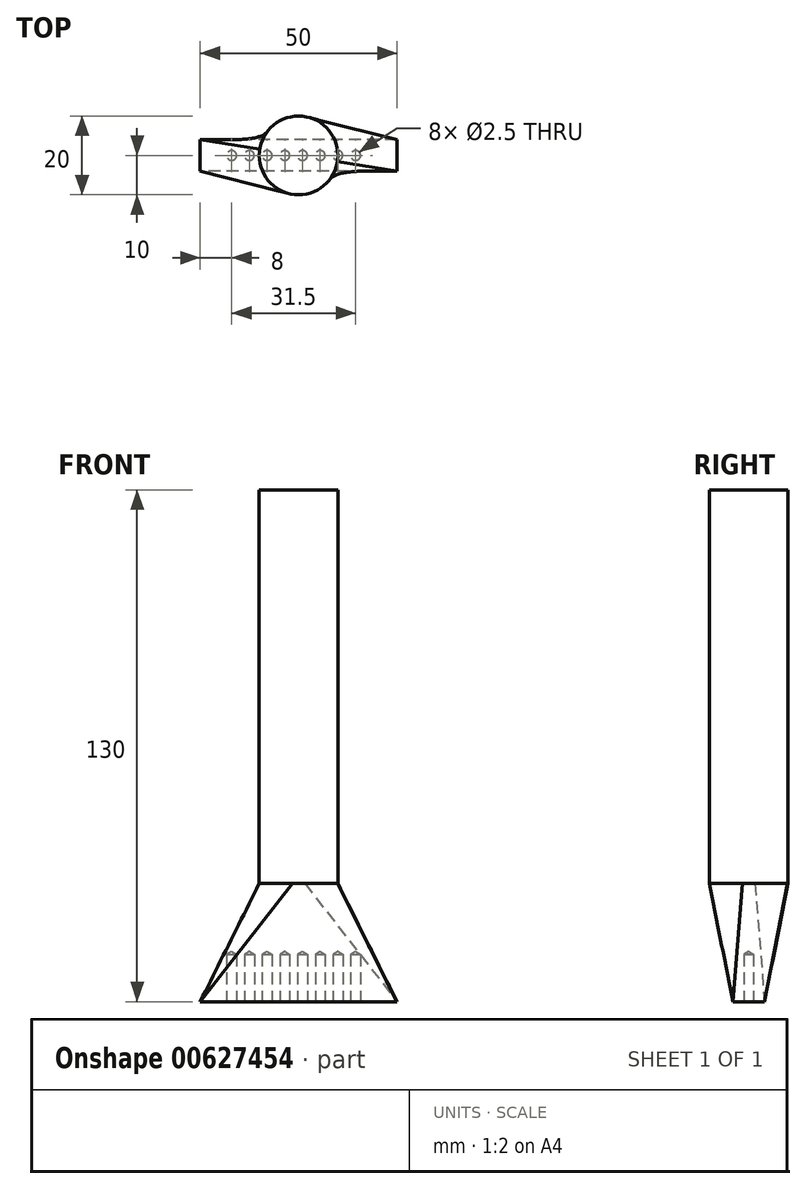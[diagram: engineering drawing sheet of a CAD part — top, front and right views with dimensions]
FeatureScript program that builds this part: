
annotation { "Feature Type Name" : "Feature", "Feature Type Description" : "" }
export const myFeature = defineFeature(function(context is Context, id is Id, definition is map)
    precondition{}
    {
        {
            var Q0;
            Q0=qCreatedBy(makeId("Top.planeOp"),FACE);
            var sketch = newSketch(context, id + "F0", { "sketchPlane" : qUnion([Q0])});
            skCircle(sketch, "E0", {"center": v(0, 0) * mm, "radius": 10 * mm});
            skSolve(sketch);
        }
        {
            var Q0;
            Q0=makeQuery(id+"F0.imprint","IMPRINT",FACE,{"disambiguationData":[TD([[makeQuery(id+"F0.imprint","IMPRINT",EDGE,{"derivedFrom":sQuery(id+"F0.wireOp",EDGE,"E0")}),1.0]])]});
            extrude(context, id + "F1", {"entities" : qUnion([Q0]), "endBound" : BoundingType.SYMMETRIC, "depth" : 100 * mm, "offsetDistance" : 25.4 * mm});
        }
        {
            var Q0;
            Q0=makeQuery(id+"F1.opExtrude","CAP_FACE",FACE,{"disambiguationData":[OSD([sQuery(id+"F0.wireOp",EDGE,"E0")])],"isStart":true});
            var sketch = newSketch(context, id + "F2", { "sketchPlane" : qUnion([Q0])});
            skCircle(sketch, "E1", {"center": v(0, 0) * mm, "radius": 10 * mm});
            skSolve(sketch);
        }
        {
            var Q0;
            Q0=makeQuery(id+"F2.imprint","IMPRINT",FACE,{"disambiguationData":[TD([[makeQuery(id+"F2.imprint","IMPRINT",EDGE,{"derivedFrom":sQuery(id+"F2.wireOp",EDGE,"E1")}),-1.0]])]});
            cPlane(context, id + "F3", {"entities" : qUnion([Q0]), "cplaneType" : CPlaneType.OFFSET, "offset" : 30 * mm, "width" : 152.4 * mm, "height" : 152.4 * mm});
        }
        {
            var Q0;
            Q0=qCreatedBy(id+"F3.planeOp",FACE);
            var sketch = newSketch(context, id + "F4", { "sketchPlane" : qUnion([Q0])});
            skLineSegment(sketch, "E2.bottom", {"start": v(25, 4) * mm, "end": v(-25, 4) * mm});
            skLineSegment(sketch, "E2.top", {"start": v(25, -4) * mm, "end": v(-25, -4) * mm});
            skLineSegment(sketch, "E2.left", {"start": v(25, 4) * mm, "end": v(25, -4) * mm});
            skLineSegment(sketch, "E2.right", {"start": v(-25, 4) * mm, "end": v(-25, -4) * mm});
            skPoint(sketch, "E2.middle", {"position": v(0, 0) * mm});
            skSolve(sketch);
        }
        {
            var Q0;
            Q0=makeQuery(id+"F2.imprint","IMPRINT",FACE,{"disambiguationData":[TD([[makeQuery(id+"F2.imprint","IMPRINT",EDGE,{"derivedFrom":sQuery(id+"F2.wireOp",EDGE,"E1")}),-1.0]])]});
            var Q1;
            Q1=makeQuery(id+"F4.imprint","IMPRINT",FACE,{"disambiguationData":[TD([[makeQuery(id+"F4.imprint","IMPRINT",EDGE,{"derivedFrom":sQuery(id+"F4.wireOp",EDGE,"E2.bottom")}),1.0]])]});
            loft(context, id + "F5", {"sheetProfilesArray" : [{ "sheetProfileEntities" : qUnion([Q0]) }, { "sheetProfileEntities" : qUnion([Q1]) }]});
        }
        {
            var Q0;
            Q0=makeQuery(id+"F5.opLoft","CAP_FACE",FACE,{"disambiguationData":[OSD([makeQuery(id+"F4.imprint","IMPRINT",FACE,{"disambiguationData":[TD([[makeQuery(id+"F4.imprint","IMPRINT",EDGE,{"derivedFrom":sQuery(id+"F4.wireOp",EDGE,"E2.bottom")}),1.0]])]})])],"isStart":true});
            var sketch = newSketch(context, id + "F6", { "sketchPlane" : qUnion([Q0])});
            skCircle(sketch, "E3", {"center": v(-17, 0) * mm, "radius": 0.5 * mm});
            skCircle(sketch, "E4.1.0.0", {"center": v(-12.5, 0) * mm, "radius": 0.5 * mm});
            skCircle(sketch, "E4.2.0.0", {"center": v(-8, 0) * mm, "radius": 0.5 * mm});
            skCircle(sketch, "E4.3.0.0", {"center": v(-3.5, 0) * mm, "radius": 0.5 * mm});
            skCircle(sketch, "E4.4.0.0", {"center": v(1, 0) * mm, "radius": 0.5 * mm});
            skCircle(sketch, "E4.5.0.0", {"center": v(5.5, 0) * mm, "radius": 0.5 * mm});
            skCircle(sketch, "E4.6.0.0", {"center": v(10, 0) * mm, "radius": 0.5 * mm});
            skCircle(sketch, "E4.7.0.0", {"center": v(14.5, 0) * mm, "radius": 0.5 * mm});
            skLineSegment(sketch, "E4.direction1", {"start": v(-17, 0) * mm, "end": v(-12.5, 0) * mm, "construction": true});
            skCircle(sketch, "E5.0.8.0", {"center": v(19, 0) * mm, "radius": 0.5 * mm});
            skSolve(sketch);
        }
        {
            var Q0;
            Q0=sQuery(id+"F6.wireOp",VERTEX,"E4.direction1.start");
            var Q1;
            Q1=sQuery(id+"F6.wireOp",VERTEX,"E4.1.0.0.center");
            var Q2;
            Q2=sQuery(id+"F6.wireOp",VERTEX,"E4.2.0.0.center");
            var Q3;
            Q3=sQuery(id+"F6.wireOp",VERTEX,"E4.3.0.0.center");
            var Q4;
            Q4=sQuery(id+"F6.wireOp",VERTEX,"E4.4.0.0.center");
            var Q5;
            Q5=sQuery(id+"F6.wireOp",VERTEX,"E4.5.0.0.center");
            var Q6;
            Q6=sQuery(id+"F6.wireOp",VERTEX,"E4.6.0.0.center");
            var Q7;
            Q7=sQuery(id+"F6.wireOp",VERTEX,"E4.7.0.0.center");
            var Q8;
            Q8=sQuery(id+"F6.wireOp",VERTEX,"E4.8.0.0.center");
            var Q9;
            Q9=sQuery(id+"F6.wireOp",VERTEX,"E4.9.0.0.center");
            var Q10;
            Q10=makeQuery(id+"F5.opLoft","SWEPT_BODY",BODY,{"disambiguationData":[OSD([makeQuery(id+"F2.imprint","IMPRINT",FACE,{"disambiguationData":[TD([[makeQuery(id+"F2.imprint","IMPRINT",EDGE,{"derivedFrom":sQuery(id+"F2.wireOp",EDGE,"E1")}),-1.0]])]}),makeQuery(id+"F4.imprint","IMPRINT",FACE,{"disambiguationData":[TD([[makeQuery(id+"F4.imprint","IMPRINT",EDGE,{"derivedFrom":sQuery(id+"F4.wireOp",EDGE,"E2.bottom")}),1.0]])]})])]});
            hole(context, id + "F7", {"style" : HoleStyle.SIMPLE, "endStyle" : HoleEndStyle.BLIND, "holeDiameter" : 2.5 * mm, "majorDiameter" : 6.35 * mm, "holeDepth" : 12 * mm, "isTappedThrough" : true, "tappedDepth" : 12.7 * mm, "tapClearance" : 3, "locations" : qUnion([Q0, Q1, Q2, Q3, Q4, Q5, Q6, Q7, Q8, Q9]), "scope" : qUnion([Q10])});
        }
    });
